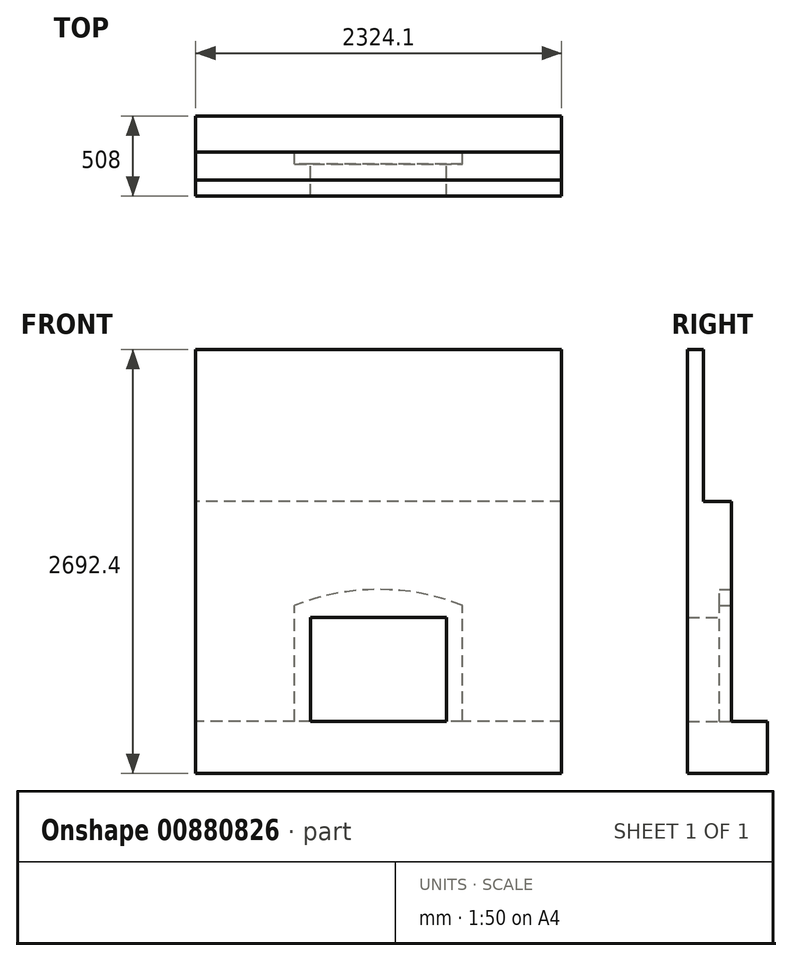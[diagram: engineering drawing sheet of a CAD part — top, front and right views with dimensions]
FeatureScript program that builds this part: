
annotation { "Feature Type Name" : "Feature", "Feature Type Description" : "" }
export const myFeature = defineFeature(function(context is Context, id is Id, definition is map)
    precondition{}
    {
        {
            var Q0;
            Q0=qCreatedBy(makeId("Top.planeOp"),FACE);
            var sketch = newSketch(context, id + "F0", { "sketchPlane" : qUnion([Q0])});
            skLineSegment(sketch, "E0.bottom", {"start": v(-1162.05, 254) * mm, "end": v(1162.05, 254) * mm});
            skLineSegment(sketch, "E0.top", {"start": v(-1162.05, -254) * mm, "end": v(1162.05, -254) * mm});
            skLineSegment(sketch, "E0.left", {"start": v(-1162.05, 254) * mm, "end": v(-1162.05, -254) * mm});
            skLineSegment(sketch, "E0.right", {"start": v(1162.05, 254) * mm, "end": v(1162.05, -254) * mm});
            skPoint(sketch, "E0.middle", {"position": v(0, 0) * mm});
            skLineSegment(sketch, "E1", {"start": v(1162.05, -254) * mm, "end": v(1162.05, -152.4) * mm});
            skLineSegment(sketch, "E2", {"start": v(1162.05, -254) * mm, "end": v(1162.05, 25.4) * mm});
            skLineSegment(sketch, "E3", {"start": v(1162.05, -152.4) * mm, "end": v(1162.05, 25.4) * mm});
            skLineSegment(sketch, "E4", {"start": v(1162.05, 25.4) * mm, "end": v(1162.05, 254) * mm});
            skLineSegment(sketch, "E5", {"start": v(1162.05, 25.4) * mm, "end": v(-1162.05, 25.4) * mm});
            skLineSegment(sketch, "E6", {"start": v(1162.05, -152.4) * mm, "end": v(-1162.05, -152.4) * mm});
            skSolve(sketch);
        }
        {
            var Q0;
            {var subQ0=sQuery(id+"F0.wireOp",EDGE,"E0.bottom");Q0=makeQuery(id+"F0.imprint","IMPRINT",FACE,{"disambiguationData":[TD([[makeQuery(id+"F0.imprint","IMPRINT",EDGE,{"derivedFrom":subQ0}),-1.0]])]});}
            extrude(context, id + "F1", {"entities" : qUnion([Q0]), "depth" : 330.2 * mm, "offsetDistance" : 25.4 * mm});
        }
        {
            var Q0;
            {var subQ0=sQuery(id+"F0.wireOp",EDGE,"E5");Q0=makeQuery(id+"F0.imprint","IMPRINT",FACE,{"disambiguationData":[TD([[makeQuery(id+"F0.imprint","IMPRINT",EDGE,{"derivedFrom":subQ0}),1.0]])]});}
            extrude(context, id + "F2", {"entities" : qUnion([Q0]), "operationType" : NewBodyOperationType.ADD, "depth" : 1727.2 * mm, "offsetDistance" : 25.4 * mm});
        }
        {
            var Q0;
            {var subQ0=sQuery(id+"F0.wireOp",EDGE,"E0.top");Q0=makeQuery(id+"F0.imprint","IMPRINT",FACE,{"disambiguationData":[TD([[makeQuery(id+"F0.imprint","IMPRINT",EDGE,{"derivedFrom":subQ0}),1.0]])]});}
            extrude(context, id + "F3", {"entities" : qUnion([Q0]), "operationType" : NewBodyOperationType.ADD, "depth" : 2692.4 * mm, "offsetDistance" : 25.4 * mm});
        }
        {
            var Q0;
            Q0=makeQuery(id+"F2.opExtrude","SWEPT_FACE",FACE,{"disambiguationData":[OSD([sQuery(id+"F0.wireOp",EDGE,"E5")])]});
            var sketch = newSketch(context, id + "F4", { "sketchPlane" : qUnion([Q0])});
            skLineSegment(sketch, "E7", {"start": v(-1162.05, 330.2) * mm, "end": v(-431.8, 330.2) * mm});
            skLineSegment(sketch, "E8", {"start": v(1162.05, 330.2) * mm, "end": v(431.8, 330.2) * mm});
            skLineSegment(sketch, "E9.bottom", {"start": v(-431.8, 330.2) * mm, "end": v(431.8, 330.2) * mm});
            skLineSegment(sketch, "E9.top", {"start": v(-431.8, 990.6) * mm, "end": v(431.8, 990.6) * mm});
            skLineSegment(sketch, "E9.left", {"start": v(-431.8, 330.2) * mm, "end": v(-431.8, 990.6) * mm});
            skLineSegment(sketch, "E9.right", {"start": v(431.8, 330.2) * mm, "end": v(431.8, 990.6) * mm});
            skLineSegment(sketch, "E10", {"start": v(-431.8, 330.2) * mm, "end": v(-533.4, 330.2) * mm});
            skLineSegment(sketch, "E11", {"start": v(431.8, 330.2) * mm, "end": v(533.4, 330.2) * mm});
            skLineSegment(sketch, "E12", {"start": v(533.4, 330.2) * mm, "end": v(431.8, 330.2) * mm});
            skLineSegment(sketch, "E13", {"start": v(-533.4, 330.2) * mm, "end": v(-533.4, 990.6) * mm});
            skLineSegment(sketch, "E14", {"start": v(-533.4, 990.6) * mm, "end": v(-533.4, 1066.8) * mm});
            skLineSegment(sketch, "E15", {"start": v(533.4, 330.2) * mm, "end": v(533.4, 990.6) * mm});
            skLineSegment(sketch, "E16", {"start": v(533.4, 990.6) * mm, "end": v(533.4, 1066.8) * mm});
            skLineSegment(sketch, "E17", {"start": v(0, 990.6) * mm, "end": v(0, 1168.4) * mm});
            skArc(sketch, "E18", {"start": v(533.4, 1066.8) * mm, "mid": v(0, 1168.4) * mm, "end": v(-533.4, 1066.8) * mm});
            skSolve(sketch);
        }
        {
            var Q0;
            Q0=makeQuery(id+"F4.imprint","IMPRINT",FACE,{"disambiguationData":[TD([[makeQuery(id+"F4.imprint","IMPRINT",EDGE,{"derivedFrom":sQuery(id+"F4.wireOp",EDGE,"E9.bottom")}),1.0]])]});
            extrude(context, id + "F5", {"entities" : qUnion([Q0]), "operationType" : NewBodyOperationType.REMOVE, "oppositeDirection" : true, "depth" : 546.1 * mm, "offsetDistance" : 25.4 * mm});
        }
        {
            var Q0;
            {var subQ0=sQuery(id+"F4.wireOp",EDGE,"E9.left");Q0=makeQuery(id+"F4.imprint","IMPRINT",FACE,{"disambiguationData":[TD([[makeQuery(id+"F4.imprint","IMPRINT",EDGE,{"derivedFrom":subQ0}),1.0]])]});}
            var Q1;
            {var subQ0=sQuery(id+"F4.wireOp",EDGE,"E9.right");Q1=makeQuery(id+"F4.imprint","IMPRINT",FACE,{"disambiguationData":[TD([[makeQuery(id+"F4.imprint","IMPRINT",EDGE,{"derivedFrom":subQ0}),-1.0]])]});}
            extrude(context, id + "F6", {"entities" : qUnion([Q0, Q1]), "operationType" : NewBodyOperationType.REMOVE, "oppositeDirection" : true, "depth" : 76.2 * mm, "offsetDistance" : 25.4 * mm});
        }
    });
